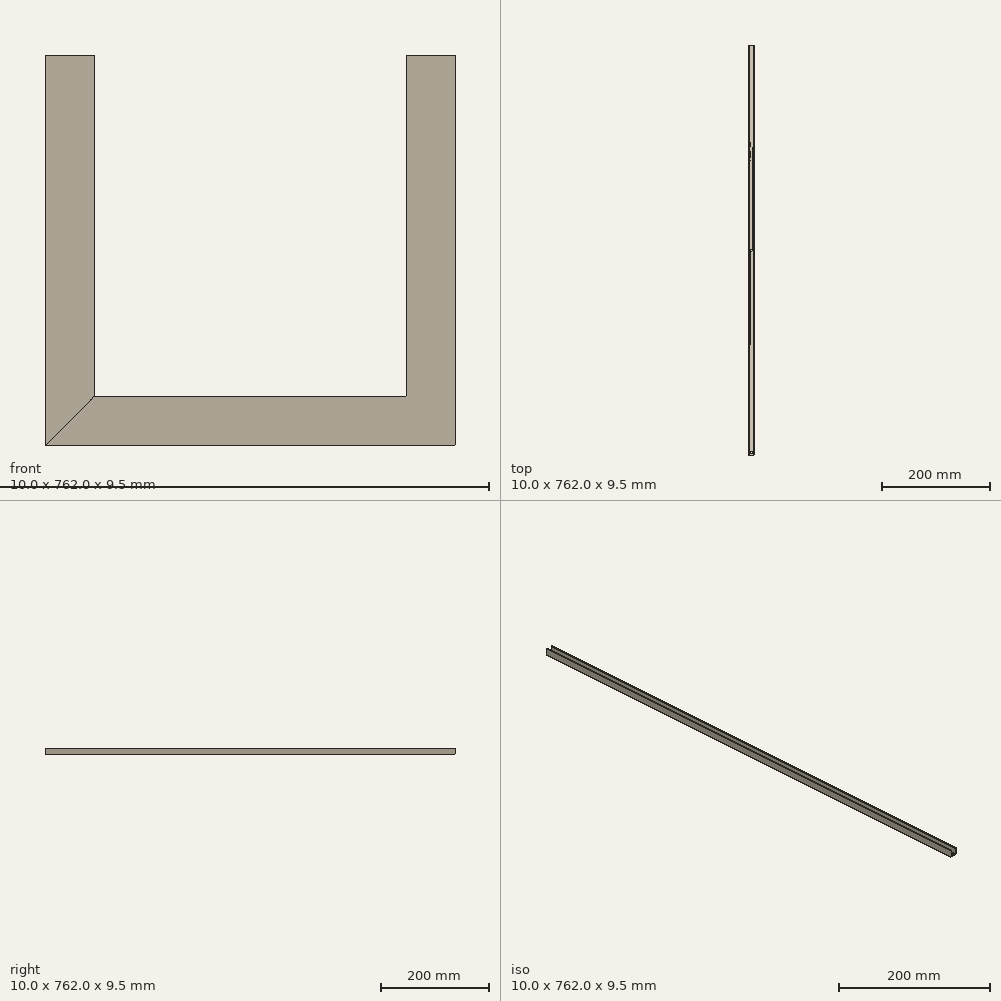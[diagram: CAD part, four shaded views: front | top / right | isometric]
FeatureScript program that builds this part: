
annotation { "Feature Type Name" : "Feature", "Feature Type Description" : "" }
export const myFeature = defineFeature(function(context is Context, id is Id, definition is map)
    precondition{}
    {
        {
            var Q0;
            Q0=qCreatedBy(makeId("Front.planeOp"),FACE);
            var sketch = newSketch(context, id + "F0", { "sketchPlane" : qUnion([Q0])});
            skLineSegment(sketch, "E0", {"start": v(-5, 9.52) * mm, "end": v(-5, 0) * mm});
            skLineSegment(sketch, "E1", {"start": v(-5, 0) * mm, "end": v(0, 0) * mm});
            skLineSegment(sketch, "E2.MirrorCS", {"start": v(5, 9.52) * mm, "end": v(5, 0) * mm});
            skLineSegment(sketch, "E3.MirrorCS", {"start": v(5, 0) * mm, "end": v(0, 0) * mm});
            skLineSegment(sketch, "E4", {"start": v(-3.8, 9.52) * mm, "end": v(-3.8, 1.2) * mm});
            skLineSegment(sketch, "E5", {"start": v(-3.8, 1.2) * mm, "end": v(3.8, 1.2) * mm});
            skLineSegment(sketch, "E6", {"start": v(3.8, 1.2) * mm, "end": v(3.8, 9.52) * mm});
            skPoint(sketch, "E7.visualSharp", {"position": v(3.8, 9.53) * mm});
            skPoint(sketch, "E8.visualSharp", {"position": v(5, 9.4) * mm});
            skLineSegment(sketch, "E9", {"start": v(-5, 9.52) * mm, "end": v(-3.8, 9.52) * mm});
            skLineSegment(sketch, "E10", {"start": v(3.8, 9.52) * mm, "end": v(5, 9.52) * mm});
            skSolve(sketch);
        }
        {
            var Q0;
            Q0=qSketchRegion(id+"F0",true);
            extrude(context, id + "F1", {"entities" : qUnion([Q0]), "depth" : 381 * mm, "hasSecondDirection" : true, "secondDirectionOppositeDirection" : true, "secondDirectionDepth" : 381 * mm});
        }
        {
            var Q0;
            Q0=makeQuery(id+"F1.opExtrude","SWEPT_FACE",FACE,{"disambiguationData":[OSD([sQuery(id+"F0.wireOp",EDGE,"E1"),sQuery(id+"F0.wireOp",EDGE,"E3.MirrorCS")])]});
            var sketch = newSketch(context, id + "F2", { "sketchPlane" : qUnion([Q0])});
            skCircle(sketch, "E11", {"center": v(0, 0) * mm, "radius": 2 * mm});
            skSolve(sketch);
        }
        {
            var Q0;
            Q0=makeQuery(id+"F2.imprint","IMPRINT",FACE,{"disambiguationData":[TD([[makeQuery(id+"F2.imprint","IMPRINT",EDGE,{"derivedFrom":sQuery(id+"F2.wireOp",EDGE,"E11")}),1.0]])]});
            extrude(context, id + "F3", {"entities" : qUnion([Q0]), "operationType" : NewBodyOperationType.REMOVE, "endBound" : BoundingType.UP_TO_NEXT, "oppositeDirection" : true, "depth" : 25 * mm});
        }
        {
            var Q0;
            Q0=makeQuery(id+"F1.opExtrude","SWEPT_FACE",FACE,{"disambiguationData":[OSD([sQuery(id+"F0.wireOp",EDGE,"E1"),sQuery(id+"F0.wireOp",EDGE,"E3.MirrorCS")])]});
            var sketch = newSketch(context, id + "F4", { "sketchPlane" : qUnion([Q0])});
            skLineSegment(sketch, "E12", {"start": v(-5, 376) * mm, "end": v(-5, 381) * mm});
            skLineSegment(sketch, "E13", {"start": v(-5, 381) * mm, "end": v(5, 381) * mm});
            skLineSegment(sketch, "E14", {"start": v(5, 381) * mm, "end": v(5, 376) * mm});
            skCircle(sketch, "E15", {"center": v(0, 376) * mm, "radius": 2 * mm});
            skSolve(sketch);
        }
        {
            var Q0;
            Q0=qSketchRegion(id+"F4",true);
            extrude(context, id + "F5", {"entities" : qUnion([Q0]), "operationType" : NewBodyOperationType.REMOVE, "endBound" : BoundingType.THROUGH_ALL, "oppositeDirection" : true, "depth" : 25 * mm});
        }
    });
